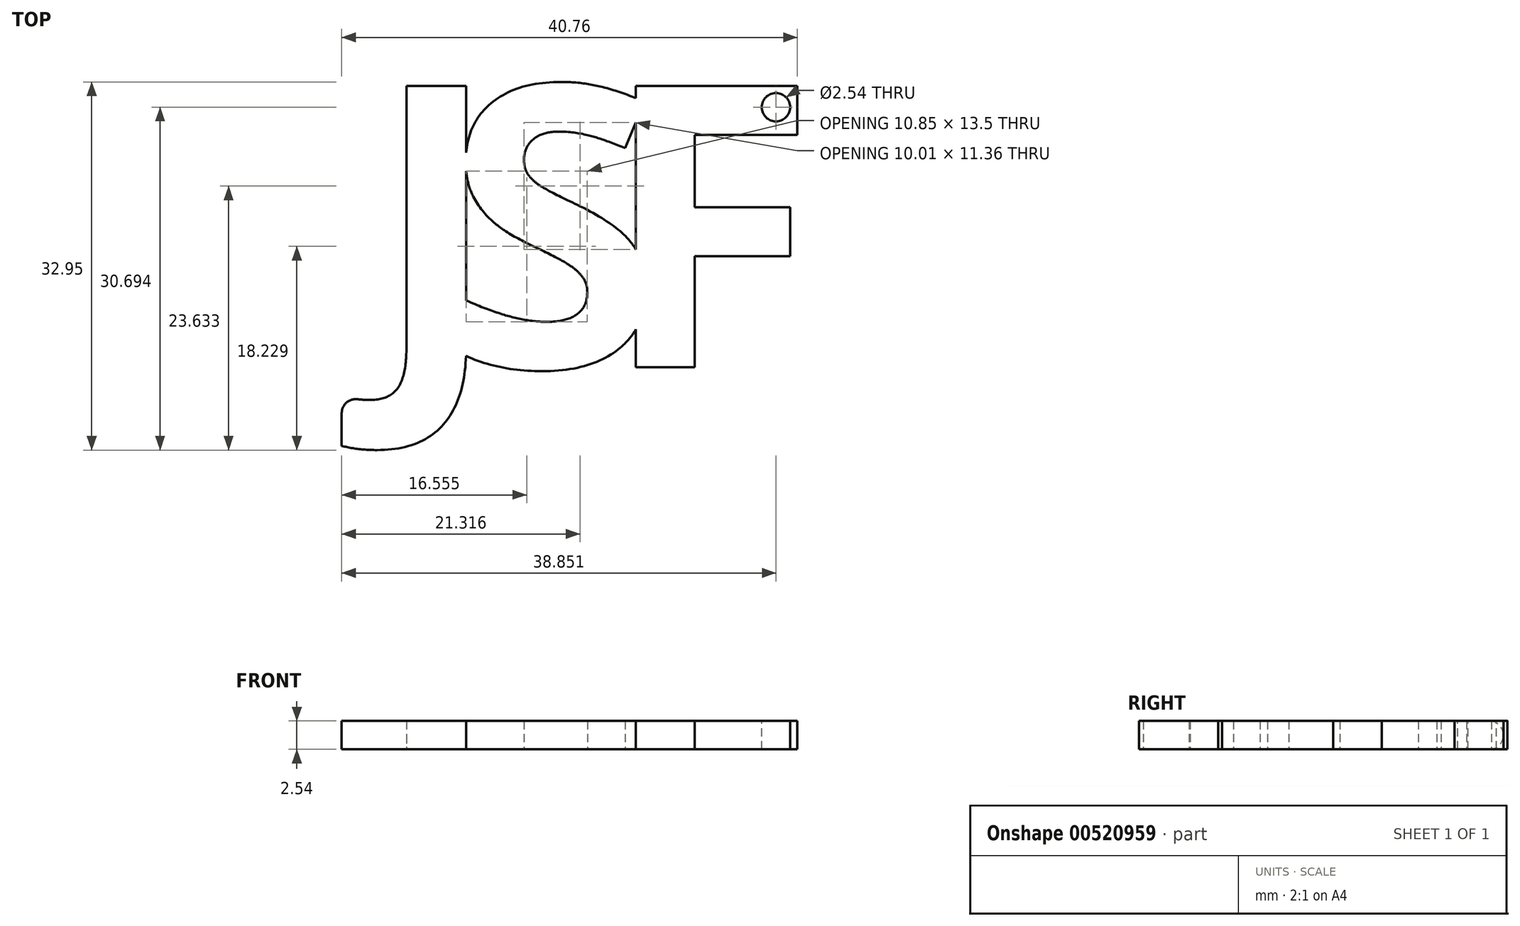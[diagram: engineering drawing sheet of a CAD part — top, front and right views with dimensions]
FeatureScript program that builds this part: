
annotation { "Feature Type Name" : "Feature", "Feature Type Description" : "" }
export const myFeature = defineFeature(function(context is Context, id is Id, definition is map)
    precondition{}
    {
        {
            var Q0;
            Q0=qCreatedBy(makeId("Top.planeOp"),FACE);
            var sketch = newSketch(context, id + "F0", { "sketchPlane" : qUnion([Q0])});
            skText(sketch, "E0", { "text": "J", "fontName": "OpenSans-Bold.ttf"});
            skText(sketch, "E1", { "text": "S", "fontName": "OpenSans-Bold.ttf"});
            skText(sketch, "E2", { "text": "F", "fontName": "OpenSans-Bold.ttf"});
            const initialGuessF0  = {"E0": [-0.03612, 0.00663, 1, 0, 0.0254], "E1": [-0.02956, 0.00663, 1, 0, 0.0254], "E2": [-0.01559, 0.00663, 1, 0, 0.0254]};
            skSetInitialGuess(sketch, initialGuessF0);
            skSolve(sketch);
        }
        {
            var Q0;
            Q0 = qSketchRegion(id + "F0", true);
            extrude(context, id + "F1", {"entities" : qUnion([Q0]), "depth" : 2.54 * mm, "offsetDistance" : 25.4 * mm});
        }
        {
            var Q0;
            Q0=makeQuery(id+"F1.opExtrude","CAP_FACE",FACE,{"disambiguationData":[OSD([sQuery(id+"F0.wireOp",EDGE,"E0.sketch_text.stroke-0"),sQuery(id+"F0.wireOp",EDGE,"E0.sketch_text.stroke-1"),sQuery(id+"F0.wireOp",EDGE,"E0.sketch_text.stroke-2"),sQuery(id+"F0.wireOp",EDGE,"E0.sketch_text.stroke-3"),sQuery(id+"F0.wireOp",EDGE,"E0.sketch_text.stroke-4"),sQuery(id+"F0.wireOp",EDGE,"E0.sketch_text.stroke-5"),sQuery(id+"F0.wireOp",EDGE,"E0.sketch_text.stroke-6"),sQuery(id+"F0.wireOp",EDGE,"E0.sketch_text.stroke-7"),sQuery(id+"F0.wireOp",EDGE,"E0.sketch_text.stroke-8"),sQuery(id+"F0.wireOp",EDGE,"E0.sketch_text.stroke-9"),sQuery(id+"F0.wireOp",EDGE,"E1.sketch_text.stroke-0"),sQuery(id+"F0.wireOp",EDGE,"E1.sketch_text.stroke-1"),sQuery(id+"F0.wireOp",EDGE,"E1.sketch_text.stroke-2"),sQuery(id+"F0.wireOp",EDGE,"E1.sketch_text.stroke-4"),sQuery(id+"F0.wireOp",EDGE,"E1.sketch_text.stroke-5"),sQuery(id+"F0.wireOp",EDGE,"E1.sketch_text.stroke-6"),sQuery(id+"F0.wireOp",EDGE,"E1.sketch_text.stroke-7"),sQuery(id+"F0.wireOp",EDGE,"E1.sketch_text.stroke-8"),sQuery(id+"F0.wireOp",EDGE,"E1.sketch_text.stroke-9"),sQuery(id+"F0.wireOp",EDGE,"E1.sketch_text.stroke-10"),sQuery(id+"F0.wireOp",EDGE,"E1.sketch_text.stroke-11"),sQuery(id+"F0.wireOp",EDGE,"E1.sketch_text.stroke-12"),sQuery(id+"F0.wireOp",EDGE,"E1.sketch_text.stroke-13"),sQuery(id+"F0.wireOp",EDGE,"E1.sketch_text.stroke-14"),sQuery(id+"F0.wireOp",EDGE,"E1.sketch_text.stroke-15"),sQuery(id+"F0.wireOp",EDGE,"E1.sketch_text.stroke-16"),sQuery(id+"F0.wireOp",EDGE,"E1.sketch_text.stroke-17"),sQuery(id+"F0.wireOp",EDGE,"E1.sketch_text.stroke-18"),sQuery(id+"F0.wireOp",EDGE,"E1.sketch_text.stroke-19"),sQuery(id+"F0.wireOp",EDGE,"E1.sketch_text.stroke-20"),sQuery(id+"F0.wireOp",EDGE,"E1.sketch_text.stroke-21"),sQuery(id+"F0.wireOp",EDGE,"E1.sketch_text.stroke-22"),sQuery(id+"F0.wireOp",EDGE,"E1.sketch_text.stroke-23"),sQuery(id+"F0.wireOp",EDGE,"E1.sketch_text.stroke-24"),sQuery(id+"F0.wireOp",EDGE,"E1.sketch_text.stroke-25"),sQuery(id+"F0.wireOp",EDGE,"E1.sketch_text.stroke-26"),sQuery(id+"F0.wireOp",EDGE,"E1.sketch_text.stroke-27"),sQuery(id+"F0.wireOp",EDGE,"E2.sketch_text.stroke-0"),sQuery(id+"F0.wireOp",EDGE,"E2.sketch_text.stroke-1"),sQuery(id+"F0.wireOp",EDGE,"E2.sketch_text.stroke-2"),sQuery(id+"F0.wireOp",EDGE,"E2.sketch_text.stroke-3"),sQuery(id+"F0.wireOp",EDGE,"E2.sketch_text.stroke-4"),sQuery(id+"F0.wireOp",EDGE,"E2.sketch_text.stroke-5"),sQuery(id+"F0.wireOp",EDGE,"E2.sketch_text.stroke-6"),sQuery(id+"F0.wireOp",EDGE,"E2.sketch_text.stroke-7"),sQuery(id+"F0.wireOp",EDGE,"E2.sketch_text.stroke-8"),sQuery(id+"F0.wireOp",EDGE,"E2.sketch_text.stroke-9")])],"isStart":false});
            var sketch = newSketch(context, id + "F2", { "sketchPlane" : qUnion([Q0])});
            skCircle(sketch, "E3", {"center": v(0.11, 29.91) * mm, "radius": 1.27 * mm});
            skSolve(sketch);
        }
        {
            var Q0;
            Q0=makeQuery(id+"F2.imprint","IMPRINT",FACE,{"disambiguationData":[TD([[makeQuery(id+"F2.imprint","IMPRINT",EDGE,{"derivedFrom":sQuery(id+"F2.wireOp",EDGE,"E3")}),1.0]])]});
            extrude(context, id + "F3", {"entities" : qUnion([Q0]), "operationType" : NewBodyOperationType.REMOVE, "oppositeDirection" : true, "depth" : 25.4 * mm, "offsetDistance" : 25.4 * mm});
        }
        {
            var Q0;
            Q0=makeQuery(id+"F1.opExtrude","CAP_EDGE",EDGE,{"disambiguationData":[OSD([sQuery(id+"F0.wireOp",EDGE,"E0.sketch_text.stroke-6")])],"isStart":false});
            fillet(context, id + "F4", {"entities" : qUnion([Q0]), "radius" : 1.27 * mm, "tangentPropagation" : true, "allowEdgeOverflow" : false});
        }
        {
            var Q0;
            Q0=makeQuery(id+"F1.opExtrude","CAP_EDGE",EDGE,{"disambiguationData":[OSD([sQuery(id+"F0.wireOp",EDGE,"E0.sketch_text.stroke-6")])],"isStart":true});
            fillet(context, id + "F5", {"entities" : qUnion([Q0]), "radius" : 1.27 * mm, "tangentPropagation" : true, "allowEdgeOverflow" : false});
        }
        {
            var Q0;
            Q0=makeQuery(id+"F1.opExtrude","SWEPT_EDGE",EDGE,{"disambiguationData":[OSD([sQuery(id+"F0.wireOp",EDGE,"E0.sketch_text.stroke-1"),sQuery(id+"F0.wireOp",EDGE,"E0.sketch_text.stroke-2")])]});
            fillet(context, id + "F6", {"entities" : qUnion([Q0]), "radius" : 1.27 * mm, "tangentPropagation" : true, "allowEdgeOverflow" : false});
        }
    });
